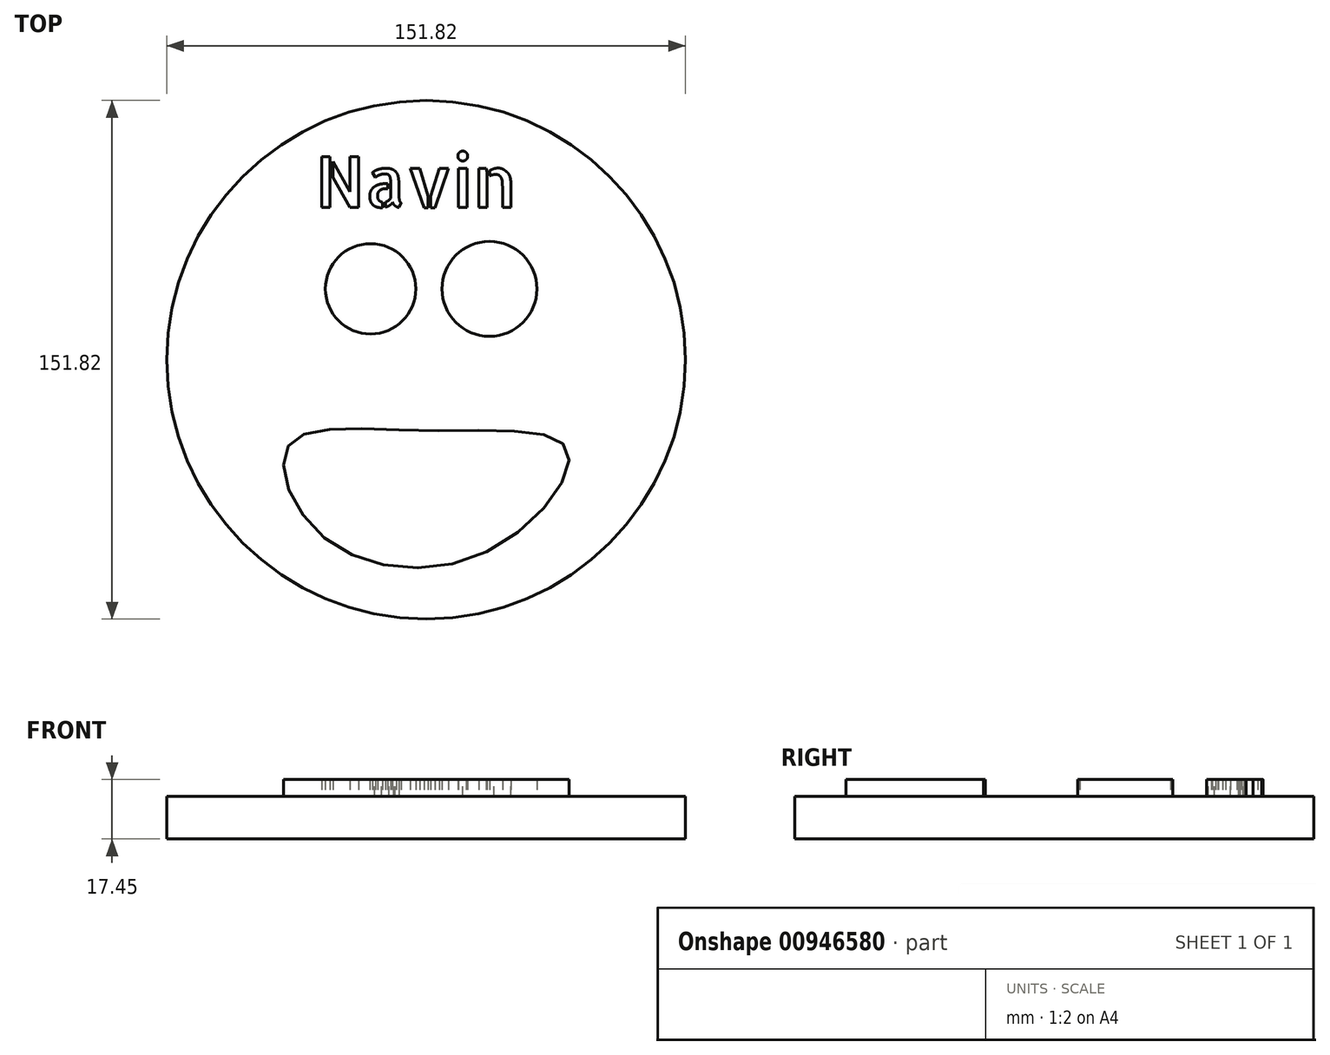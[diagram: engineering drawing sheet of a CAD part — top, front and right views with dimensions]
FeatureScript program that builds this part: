
annotation { "Feature Type Name" : "Feature", "Feature Type Description" : "" }
export const myFeature = defineFeature(function(context is Context, id is Id, definition is map)
    precondition{}
    {
        {
            var Q0;
            Q0=qCreatedBy(makeId("Top.planeOp"),FACE);
            var sketch = newSketch(context, id + "F0", { "sketchPlane" : qUnion([Q0])});
            skCircle(sketch, "E0", {"center": v(0, 0) * mm, "radius": 75.91 * mm});
            skSolve(sketch);
        }
        {
            var Q0;
            Q0 = qSketchRegion(id + "F0", true);
            extrude(context, id + "F1", {"entities" : qUnion([Q0]), "depth" : 12.45 * mm, "offsetDistance" : 25.4 * mm});
        }
        {
            var Q0;
            Q0=makeQuery(id+"F1.opExtrude","CAP_FACE",FACE,{"disambiguationData":[OSD([sQuery(id+"F0.wireOp",EDGE,"E0")])],"isStart":false});
            var sketch = newSketch(context, id + "F2", { "sketchPlane" : qUnion([Q0])});
            skCircle(sketch, "E1", {"center": v(18.51, 20.75) * mm, "radius": 13.9 * mm});
            skSolve(sketch);
        }
        {
            var Q0;
            Q0=makeQuery(id+"F2.imprint","IMPRINT",FACE,{"disambiguationData":[TD([[makeQuery(id+"F2.imprint","IMPRINT",EDGE,{"derivedFrom":sQuery(id+"F2.wireOp",EDGE,"E1")}),-1.0]])]});
            var sketch = newSketch(context, id + "F3", { "sketchPlane" : qUnion([Q0])});
            skCircle(sketch, "E2", {"center": v(-16.28, 20.75) * mm, "radius": 13.23 * mm});
            skSolve(sketch);
        }
        {
            var Q0;
            Q0=makeQuery(id+"F2.imprint","IMPRINT",FACE,{"disambiguationData":[TD([[makeQuery(id+"F2.imprint","IMPRINT",EDGE,{"derivedFrom":sQuery(id+"F2.wireOp",EDGE,"E1")}),1.0]])]});
            extrude(context, id + "F4", {"entities" : qUnion([Q0]), "operationType" : NewBodyOperationType.ADD, "depth" : 5 * mm, "offsetDistance" : 25.4 * mm});
        }
        {
            var Q0;
            Q0 = qSketchRegion(id + "F3", true);
            extrude(context, id + "F5", {"entities" : qUnion([Q0]), "operationType" : NewBodyOperationType.ADD, "depth" : 5 * mm, "offsetDistance" : 25.4 * mm});
        }
        {
            var Q0;
            Q0=makeQuery(id+"F1.opExtrude","CAP_FACE",FACE,{"disambiguationData":[OSD([sQuery(id+"F0.wireOp",EDGE,"E0")])],"isStart":false});
            var sketch = newSketch(context, id + "F6", { "sketchPlane" : qUnion([Q0])});
            skSolve(sketch);
        }
        {
            var Q0;
            Q0=makeQuery(id+"F6.imprint","IMPRINT",FACE,{"disambiguationData":[TD([[makeQuery(id+"F6.imprint","IMPRINT",EDGE,{"derivedFrom":makeQuery(id+"F1.opExtrude","CAP_EDGE",EDGE,{"disambiguationData":[OSD([sQuery(id+"F0.wireOp",EDGE,"E0")])],"isStart":false})}),1.0]])]});
            var sketch = newSketch(context, id + "F7", { "sketchPlane" : qUnion([Q0])});
            skFitSpline(sketch, "E3", {"points": [v(-40.38, -25.22) * mm, v(-30.44, -51.56) * mm, v(18.01, -56.03) * mm, v(41.37, -26.47) * mm, v(0, -20.75) * mm, v(-40.38, -25.22) * mm]});
            skSolve(sketch);
        }
        {
            var Q0;
            Q0 = qSketchRegion(id + "F7", true);
            extrude(context, id + "F8", {"entities" : qUnion([Q0]), "operationType" : NewBodyOperationType.ADD, "depth" : 5 * mm, "offsetDistance" : 25.4 * mm});
        }
        {
            var Q0;
            Q0=makeQuery(id+"F6.imprint","IMPRINT",FACE,{"disambiguationData":[TD([[makeQuery(id+"F6.imprint","IMPRINT",EDGE,{"derivedFrom":makeQuery(id+"F1.opExtrude","CAP_EDGE",EDGE,{"disambiguationData":[OSD([sQuery(id+"F0.wireOp",EDGE,"E0")])],"isStart":false})}),1.0]])]});
            var sketch = newSketch(context, id + "F9", { "sketchPlane" : qUnion([Q0])});
            skSolve(sketch);
        }
        {
            var Q0;
            Q0=makeQuery(id+"F9.imprint","IMPRINT",FACE,{"disambiguationData":[TD([[makeQuery(id+"F9.imprint","IMPRINT",EDGE,{"derivedFrom":makeQuery(id+"F6.imprint","IMPRINT",EDGE,{"derivedFrom":makeQuery(id+"F1.opExtrude","CAP_EDGE",EDGE,{"disambiguationData":[OSD([sQuery(id+"F0.wireOp",EDGE,"E0")])],"isStart":false})})}),1.0]])]});
            var sketch = newSketch(context, id + "F10", { "sketchPlane" : qUnion([Q0])});
            skText(sketch, "E4", { "text": "Navin", "fontName": "AllertaStencil-Regular.ttf"});
            const initialGuessF10  = {"E4": [-0.03243, 0.0446, 1, 0, 0.0149]};
            skSetInitialGuess(sketch, initialGuessF10);
            skSolve(sketch);
        }
        {
            var Q0;
            Q0 = qSketchRegion(id + "F10", true);
            extrude(context, id + "F11", {"entities" : qUnion([Q0]), "operationType" : NewBodyOperationType.ADD, "depth" : 5 * mm, "offsetDistance" : 25.4 * mm});
        }
    });
